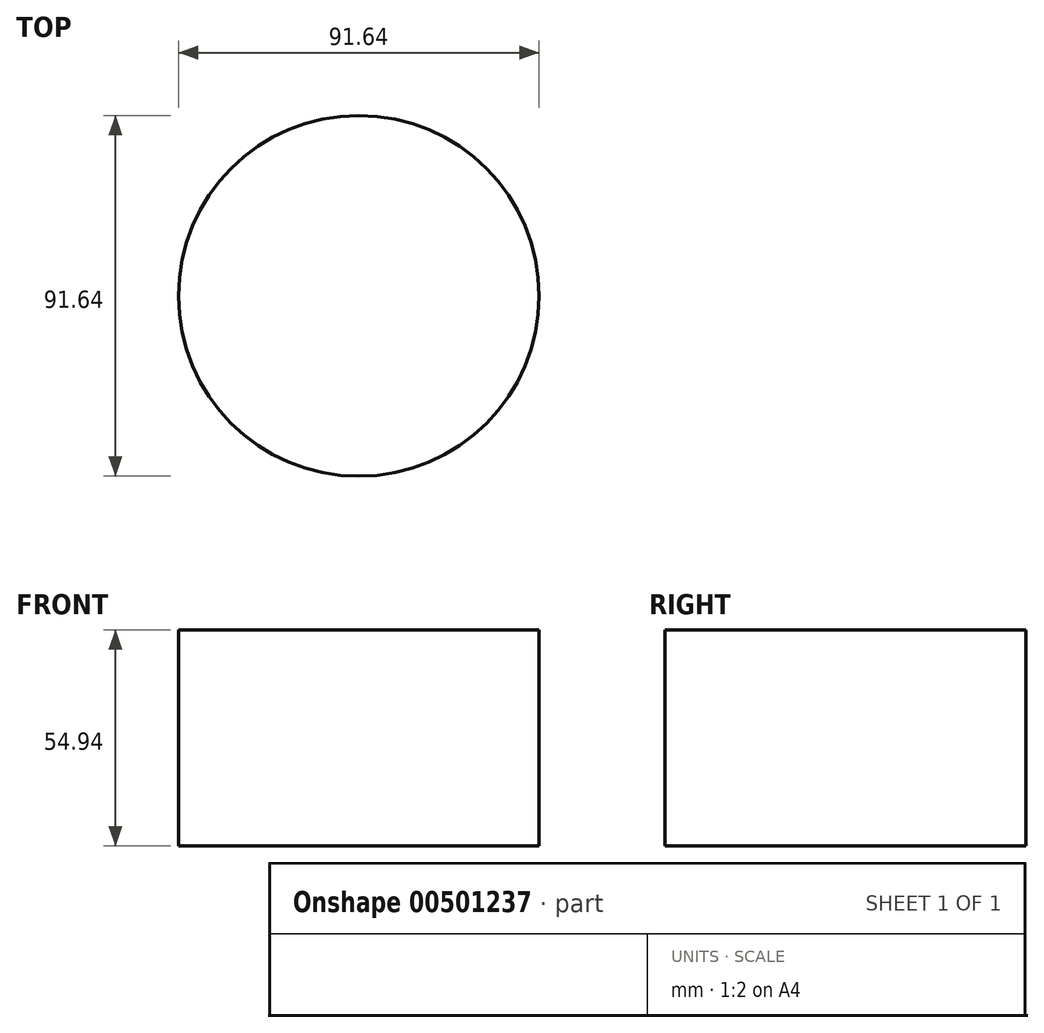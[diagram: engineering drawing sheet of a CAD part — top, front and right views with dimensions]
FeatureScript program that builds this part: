
annotation { "Feature Type Name" : "Feature", "Feature Type Description" : "" }
export const myFeature = defineFeature(function(context is Context, id is Id, definition is map)
    precondition{}
    {
        {
            var Q0;
            Q0=qCreatedBy(makeId("Top.planeOp"),FACE);
            var sketch = newSketch(context, id + "F0", { "sketchPlane" : qUnion([Q0])});
            skCircle(sketch, "E0", {"center": v(0, 0) * mm, "radius": 45.82 * mm});
            skSolve(sketch);
        }
        {
            var Q0;
            Q0 = qSketchRegion(id + "F0", true);
            extrude(context, id + "F1", {"entities" : qUnion([Q0]), "depth" : 54.94 * mm});
        }
    });
